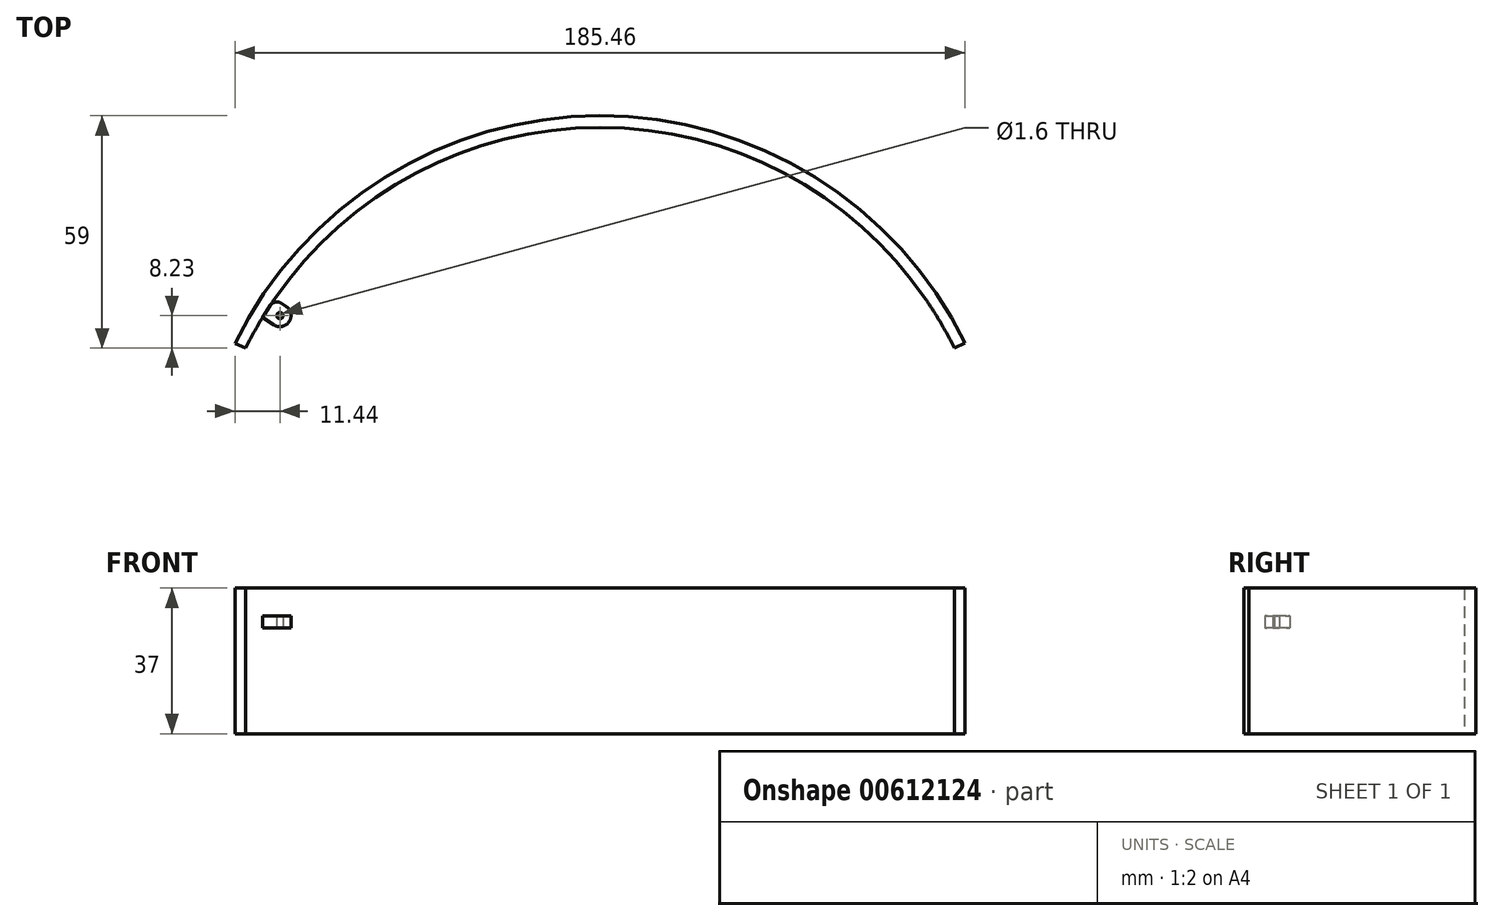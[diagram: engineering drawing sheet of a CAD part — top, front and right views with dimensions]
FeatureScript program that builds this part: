
annotation { "Feature Type Name" : "Feature", "Feature Type Description" : "" }
export const myFeature = defineFeature(function(context is Context, id is Id, definition is map)
    precondition{}
    {
        {
            var Q0;
            Q0=qCreatedBy(makeId("Top.planeOp"),FACE);
            var sketch = newSketch(context, id + "F0", { "sketchPlane" : qUnion([Q0])});
            skArc(sketch, "E0", {"start": v(90, 0) * mm, "mid": v(87.96, 3.92) * mm, "end": v(85.75, 7.76) * mm});
            skPoint(sketch, "E1", {"position": v(0, 56) * mm});
            skArc(sketch, "E2.0", {"start": v(92.7, 1.33) * mm, "mid": v(-0.07, 59) * mm, "end": v(-92.76, 1.2) * mm});
            skLineSegment(sketch, "E3", {"start": v(90, 0) * mm, "end": v(92.7, 1.33) * mm});
            skLineSegment(sketch, "E4", {"start": v(-90, 0) * mm, "end": v(-92.76, 1.2) * mm});
            skCircle(sketch, "E5", {"center": v(-81.32, 8.23) * mm, "radius": 0.8 * mm});
            skArc(sketch, "E6.0", {"start": v(-82.84, 5.88) * mm, "mid": v(-78.97, 6.7) * mm, "end": v(-79.8, 10.58) * mm});
            skLineSegment(sketch, "E7", {"start": v(-82.84, 5.88) * mm, "end": v(-85.75, 7.76) * mm});
            skLineSegment(sketch, "E8", {"start": v(-79.8, 10.58) * mm, "end": v(-82.7, 12.46) * mm});
            skLineSegment(sketch, "E9", {"start": v(-82.84, 5.88) * mm, "end": v(-79.8, 10.58) * mm, "construction": true});
            skArc(sketch, "E10.trimOffspring", {"start": v(-85.75, 7.76) * mm, "mid": v(-87.96, 3.92) * mm, "end": v(-90, 0) * mm});
            skLineSegment(sketch, "E11", {"start": v(0, 0) * mm, "end": v(0, 56) * mm, "construction": true});
            skArc(sketch, "E12.MirrorCS", {"start": v(82.84, 5.88) * mm, "mid": v(78.97, 6.7) * mm, "end": v(79.8, 10.58) * mm});
            skLineSegment(sketch, "E13.MirrorCS", {"start": v(79.8, 10.58) * mm, "end": v(82.7, 12.46) * mm});
            skLineSegment(sketch, "E14.MirrorCS", {"start": v(82.84, 5.88) * mm, "end": v(85.75, 7.76) * mm});
            skCircle(sketch, "E15.MirrorC", {"center": v(81.32, 8.23) * mm, "radius": 0.8 * mm});
            skArc(sketch, "E16.trimOffspring", {"start": v(82.7, 12.46) * mm, "mid": v(0, 56) * mm, "end": v(-82.7, 12.46) * mm});
            skSolve(sketch);
        }
        {
            var Q0;
            Q0 = qSketchRegion(id + "F0", true);
            extrude(context, id + "F1", {"entities" : qUnion([Q0]), "depth" : 37 * mm, "offsetDistance" : 25 * mm});
        }
        {
            var Q0;
            Q0=makeQuery(id+"F1.opExtrude","SWEPT_FACE",FACE,{"disambiguationData":[OSD([sQuery(id+"F0.wireOp",EDGE,"E7")])]});
            var sketch = newSketch(context, id + "F2", { "sketchPlane" : qUnion([Q0])});
            skLineSegment(sketch, "E17.bottom", {"start": v(-76.23, 26.9) * mm, "end": v(-68.34, 26.9) * mm});
            skLineSegment(sketch, "E17.top", {"start": v(-76.23, 10.1) * mm, "end": v(-68.34, 10.1) * mm});
            skLineSegment(sketch, "E17.left", {"start": v(-76.23, 26.9) * mm, "end": v(-76.23, 10.1) * mm});
            skLineSegment(sketch, "E17.right", {"start": v(-68.34, 26.9) * mm, "end": v(-68.34, 10.1) * mm});
            skPoint(sketch, "E18", {"position": v(-68.34, 18.5) * mm});
            skPoint(sketch, "E19", {"position": v(-72.77, 18.5) * mm});
            skSolve(sketch);
        }
        {
            var Q0;
            Q0 = qSketchRegion(id + "F2", true);
            var Q1;
            Q1=makeQuery(id+"F1.opExtrude","SWEPT_FACE",FACE,{"disambiguationData":[OSD([sQuery(id+"F0.wireOp",EDGE,"E16.trimOffspring")])]});
            extrude(context, id + "F3", {"entities" : qUnion([Q0]), "operationType" : NewBodyOperationType.REMOVE, "endBound" : BoundingType.UP_TO_SURFACE, "oppositeDirection" : true, "depth" : 25 * mm, "endBoundEntityFace" : qUnion([Q1]), "offsetDistance" : 25 * mm});
        }
        {
            var Q0;
            Q0=makeQuery(id+"F1.opExtrude","CAP_FACE",FACE,{"disambiguationData":[OSD([sQuery(id+"F0.wireOp",EDGE,"E0"),sQuery(id+"F0.wireOp",EDGE,"E2.0"),sQuery(id+"F0.wireOp",EDGE,"E3"),sQuery(id+"F0.wireOp",EDGE,"E4"),sQuery(id+"F0.wireOp",EDGE,"E5"),sQuery(id+"F0.wireOp",EDGE,"E6.0"),sQuery(id+"F0.wireOp",EDGE,"E7"),sQuery(id+"F0.wireOp",EDGE,"E8"),sQuery(id+"F0.wireOp",EDGE,"E10.trimOffspring"),sQuery(id+"F0.wireOp",EDGE,"E12.MirrorCS"),sQuery(id+"F0.wireOp",EDGE,"E13.MirrorCS"),sQuery(id+"F0.wireOp",EDGE,"E14.MirrorCS"),sQuery(id+"F0.wireOp",EDGE,"E15.MirrorC"),sQuery(id+"F0.wireOp",EDGE,"E16.trimOffspring")])],"isStart":false});
            var sketch = newSketch(context, id + "F4", { "sketchPlane" : qUnion([Q0])});
            skArc(sketch, "E20.0", {"start": v(-82.84, 5.88) * mm, "mid": v(-78.97, 6.7) * mm, "end": v(-79.8, 10.58) * mm});
            skPoint(sketch, "E21.0", {"position": v(-81.25, 11.52) * mm});
            skLineSegment(sketch, "E22.0", {"start": v(-79.8, 10.58) * mm, "end": v(-82.7, 12.46) * mm});
            skLineSegment(sketch, "E23.0", {"start": v(-82.84, 5.88) * mm, "end": v(-85.75, 7.76) * mm});
            skArc(sketch, "E24.0", {"start": v(-82.7, 12.46) * mm, "mid": v(-84.26, 10.13) * mm, "end": v(-85.75, 7.76) * mm});
            skLineSegment(sketch, "E25.0", {"start": v(79.8, 10.58) * mm, "end": v(82.7, 12.46) * mm});
            skArc(sketch, "E26.0", {"start": v(82.84, 5.88) * mm, "mid": v(78.97, 6.7) * mm, "end": v(79.8, 10.58) * mm});
            skLineSegment(sketch, "E27.0", {"start": v(82.84, 5.88) * mm, "end": v(85.75, 7.76) * mm});
            skArc(sketch, "E28.0", {"start": v(85.75, 7.76) * mm, "mid": v(84.26, 10.13) * mm, "end": v(82.7, 12.46) * mm});
            skPoint(sketch, "E29.orphan", {"position": v(-90, 0) * mm});
            skPoint(sketch, "E30.orphan", {"position": v(90, 0) * mm});
            skSolve(sketch);
        }
        {
            var Q0;
            Q0 = qSketchRegion(id + "F4", true);
            extrude(context, id + "F5", {"entities" : qUnion([Q0]), "operationType" : NewBodyOperationType.REMOVE, "endBound" : BoundingType.UP_TO_NEXT, "oppositeDirection" : true, "depth" : 25 * mm, "hasOffset" : true, "offsetDistance" : 3 * mm});
        }
        {
            var Q0;
            Q0=makeQuery(id+"F1.opExtrude","CAP_FACE",FACE,{"disambiguationData":[OSD([sQuery(id+"F0.wireOp",EDGE,"E0"),sQuery(id+"F0.wireOp",EDGE,"E2.0"),sQuery(id+"F0.wireOp",EDGE,"E3"),sQuery(id+"F0.wireOp",EDGE,"E4"),sQuery(id+"F0.wireOp",EDGE,"E5"),sQuery(id+"F0.wireOp",EDGE,"E6.0"),sQuery(id+"F0.wireOp",EDGE,"E7"),sQuery(id+"F0.wireOp",EDGE,"E8"),sQuery(id+"F0.wireOp",EDGE,"E10.trimOffspring"),sQuery(id+"F0.wireOp",EDGE,"E12.MirrorCS"),sQuery(id+"F0.wireOp",EDGE,"E13.MirrorCS"),sQuery(id+"F0.wireOp",EDGE,"E14.MirrorCS"),sQuery(id+"F0.wireOp",EDGE,"E15.MirrorC"),sQuery(id+"F0.wireOp",EDGE,"E16.trimOffspring")])],"isStart":true});
            var sketch = newSketch(context, id + "F6", { "sketchPlane" : qUnion([Q0])});
            skArc(sketch, "E31.0", {"start": v(-82.7, -12.46) * mm, "mid": v(-84.26, -10.13) * mm, "end": v(-85.75, -7.76) * mm});
            skLineSegment(sketch, "E32.0", {"start": v(-82.84, -5.88) * mm, "end": v(-85.75, -7.76) * mm});
            skArc(sketch, "E33.0", {"start": v(-82.84, -5.88) * mm, "mid": v(-78.97, -6.7) * mm, "end": v(-79.8, -10.58) * mm});
            skLineSegment(sketch, "E34.0", {"start": v(-79.8, -10.58) * mm, "end": v(-82.7, -12.46) * mm});
            skArc(sketch, "E35.0", {"start": v(85.75, -7.76) * mm, "mid": v(84.26, -10.13) * mm, "end": v(82.7, -12.46) * mm});
            skLineSegment(sketch, "E36.0", {"start": v(82.84, -5.88) * mm, "end": v(85.75, -7.76) * mm});
            skArc(sketch, "E37.0", {"start": v(82.84, -5.88) * mm, "mid": v(78.97, -6.7) * mm, "end": v(79.8, -10.58) * mm});
            skLineSegment(sketch, "E38.0", {"start": v(79.8, -10.58) * mm, "end": v(82.7, -12.46) * mm});
            skSolve(sketch);
        }
        {
            var Q0;
            Q0 = qSketchRegion(id + "F6", true);
            extrude(context, id + "F7", {"entities" : qUnion([Q0]), "operationType" : NewBodyOperationType.REMOVE, "oppositeDirection" : true, "depth" : 7.1 * mm, "hasOffset" : true, "offsetDistance" : 3 * mm});
        }
        {
            var Q0;
            {var subQ0=sQuery(id+"F0.wireOp",EDGE,"E10.trimOffspring");var subQ1=sQuery(id+"F0.wireOp",EDGE,"E7");Q0=makeQuery(id+"F3.boolean.opBoolean","SPLIT",EDGE,{"disambiguationData":[TD([makeQuery(id+"F3.opExtrude","SWEPT_FACE",FACE,{"disambiguationData":[OSD([sQuery(id+"F2.wireOp",EDGE,"E17.bottom")])]})])],"derivedFrom":makeQuery(id+"F1.opExtrude","SWEPT_EDGE",EDGE,{"disambiguationData":[OSD([subQ1,subQ0])]})});}
            var Q1;
            {var subQ0=sQuery(id+"F0.wireOp",EDGE,"E10.trimOffspring");var subQ1=sQuery(id+"F0.wireOp",EDGE,"E7");Q1=makeQuery(id+"F3.boolean.opBoolean","SPLIT",EDGE,{"disambiguationData":[TD([makeQuery(id+"F3.opExtrude","SWEPT_FACE",FACE,{"disambiguationData":[OSD([sQuery(id+"F2.wireOp",EDGE,"E17.top")])]})])],"derivedFrom":makeQuery(id+"F1.opExtrude","SWEPT_EDGE",EDGE,{"disambiguationData":[OSD([subQ1,subQ0])]})});}
            var Q2;
            {var subQ0=sQuery(id+"F0.wireOp",EDGE,"E16.trimOffspring");var subQ1=sQuery(id+"F0.wireOp",EDGE,"E8");Q2=makeQuery(id+"F3.boolean.opBoolean","SPLIT",EDGE,{"disambiguationData":[TD([makeQuery(id+"F3.opExtrude","SWEPT_FACE",FACE,{"disambiguationData":[OSD([sQuery(id+"F2.wireOp",EDGE,"E17.top")])]})])],"derivedFrom":makeQuery(id+"F1.opExtrude","SWEPT_EDGE",EDGE,{"disambiguationData":[OSD([subQ1,subQ0])]})});}
            var Q3;
            {var subQ0=sQuery(id+"F0.wireOp",EDGE,"E16.trimOffspring");var subQ1=sQuery(id+"F0.wireOp",EDGE,"E8");Q3=makeQuery(id+"F3.boolean.opBoolean","SPLIT",EDGE,{"disambiguationData":[TD([makeQuery(id+"F3.opExtrude","SWEPT_FACE",FACE,{"disambiguationData":[OSD([sQuery(id+"F2.wireOp",EDGE,"E17.bottom")])]})])],"derivedFrom":makeQuery(id+"F1.opExtrude","SWEPT_EDGE",EDGE,{"disambiguationData":[OSD([subQ1,subQ0])]})});}
            var Q4;
            {var subQ0=sQuery(id+"F0.wireOp",EDGE,"E14.MirrorCS");var subQ1=sQuery(id+"F0.wireOp",EDGE,"E0");Q4=makeQuery(id+"FS2PbDrXnQPpyPn_1.1.F3.boolean.opBoolean","SPLIT",EDGE,{"disambiguationData":[TD([makeQuery(id+"FS2PbDrXnQPpyPn_1.1.F3.opExtrude","SWEPT_FACE",FACE,{"disambiguationData":[OSD([sQuery(id+"F2.wireOp",EDGE,"E17.bottom")])]})])],"derivedFrom":makeQuery(id+"F1.opExtrude","SWEPT_EDGE",EDGE,{"disambiguationData":[OSD([subQ1,subQ0])]})});}
            var Q5;
            {var subQ0=sQuery(id+"F0.wireOp",EDGE,"E0");var subQ1=sQuery(id+"F0.wireOp",EDGE,"E14.MirrorCS");Q5=makeQuery(id+"FS2PbDrXnQPpyPn_1.1.F3.boolean.opBoolean","SPLIT",EDGE,{"disambiguationData":[TD([makeQuery(id+"FS2PbDrXnQPpyPn_1.1.F3.opExtrude","SWEPT_FACE",FACE,{"disambiguationData":[OSD([sQuery(id+"F2.wireOp",EDGE,"E17.top")])]})])],"derivedFrom":makeQuery(id+"F1.opExtrude","SWEPT_EDGE",EDGE,{"disambiguationData":[OSD([subQ0,subQ1])]})});}
            var Q6;
            {var subQ0=sQuery(id+"F0.wireOp",EDGE,"E16.trimOffspring");var subQ1=sQuery(id+"F0.wireOp",EDGE,"E13.MirrorCS");Q6=makeQuery(id+"FS2PbDrXnQPpyPn_1.1.F3.boolean.opBoolean","SPLIT",EDGE,{"disambiguationData":[TD([makeQuery(id+"FS2PbDrXnQPpyPn_1.1.F3.opExtrude","SWEPT_FACE",FACE,{"disambiguationData":[OSD([sQuery(id+"F2.wireOp",EDGE,"E17.top")])]})])],"derivedFrom":makeQuery(id+"F1.opExtrude","SWEPT_EDGE",EDGE,{"disambiguationData":[OSD([subQ1,subQ0])]})});}
            var Q7;
            {var subQ0=sQuery(id+"F0.wireOp",EDGE,"E16.trimOffspring");var subQ1=sQuery(id+"F0.wireOp",EDGE,"E13.MirrorCS");Q7=makeQuery(id+"FS2PbDrXnQPpyPn_1.1.F3.boolean.opBoolean","SPLIT",EDGE,{"disambiguationData":[TD([makeQuery(id+"FS2PbDrXnQPpyPn_1.1.F3.opExtrude","SWEPT_FACE",FACE,{"disambiguationData":[OSD([sQuery(id+"F2.wireOp",EDGE,"E17.bottom")])]})])],"derivedFrom":makeQuery(id+"F1.opExtrude","SWEPT_EDGE",EDGE,{"disambiguationData":[OSD([subQ1,subQ0])]})});}
            fillet(context, id + "F8", {"entities" : qUnion([Q0, Q1, Q2, Q3, Q4, Q5, Q6, Q7]), "radius" : 2 * mm, "tangentPropagation" : true, "allowEdgeOverflow" : false});
        }
    });
